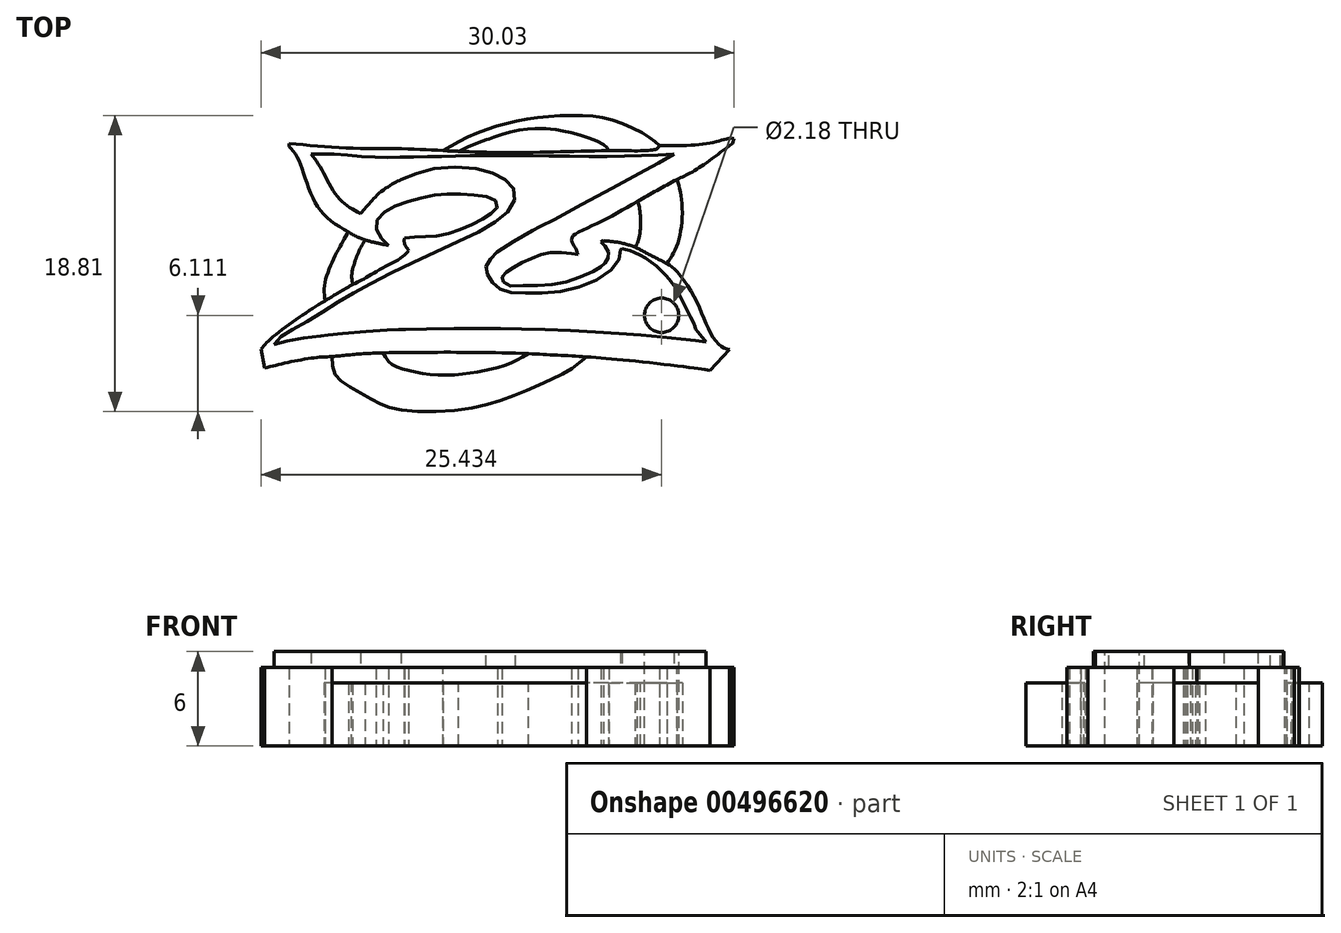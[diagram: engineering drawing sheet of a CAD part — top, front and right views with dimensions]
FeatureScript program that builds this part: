
annotation { "Feature Type Name" : "Feature", "Feature Type Description" : "" }
export const myFeature = defineFeature(function(context is Context, id is Id, definition is map)
    precondition{}
    {
        {
            var Q0;
            Q0=qCreatedBy(makeId("Top.planeOp"),FACE);
            var sketch = newSketch(context, id + "F0", { "sketchPlane" : qUnion([Q0])});
            skFitSpline(sketch, "E0", {"points": [v(13.58, 13.35) * mm, v(13.14, 12.61) * mm, v(12.53, 11.4) * mm, v(12.07, 10.03) * mm, v(12.1, 8.98) * mm], "startDerivative": vector(-2, -3.2) * mm, "endDerivative": vector(0.48, -4.3) * mm});
            skFitSpline(sketch, "E1", {"points": [v(12.1, 8.98) * mm, v(10.27, 7.8) * mm, v(8.5, 6.45) * mm, v(8.04, 5.92) * mm], "startDerivative": vector(-4.56, -2.82) * mm, "endDerivative": vector(-1.64, -2.15) * mm});
            skFitSpline(sketch, "E2", {"points": [v(8.04, 5.92) * mm, v(8.25, 4.7) * mm], "startDerivative": vector(0.2, -1.22) * mm, "endDerivative": vector(0.2, -1.22) * mm});
            skFitSpline(sketch, "E3", {"points": [v(8.25, 4.7) * mm, v(9.7, 5.06) * mm, v(11.49, 5.38) * mm, v(12.53, 5.44) * mm], "startDerivative": vector(4.05, 1.06) * mm, "endDerivative": vector(3.4, 0.09) * mm});
            skFitSpline(sketch, "E4", {"points": [v(12.53, 5.44) * mm, v(12.72, 4.35) * mm, v(13.67, 3.5) * mm, v(15.35, 2.58) * mm, v(16.7, 2.08) * mm, v(20.78, 2.08) * mm, v(23.76, 2.84) * mm, v(26.09, 3.8) * mm, v(27.8, 4.7) * mm, v(28.7, 5.43) * mm], "startDerivative": vector(0.47, -13.97) * mm, "endDerivative": vector(9.33, 8.63) * mm});
            skFitSpline(sketch, "E5", {"points": [v(28.7, 5.43) * mm, v(31.5, 5.19) * mm, v(35.57, 4.7) * mm, v(36.54, 4.55) * mm], "startDerivative": vector(7.06, -0.54) * mm, "endDerivative": vector(3.65, -0.63) * mm});
            skFitSpline(sketch, "E6", {"points": [v(36.54, 4.55) * mm, v(37.79, 5.9) * mm], "startDerivative": vector(1.1, 1.19) * mm, "endDerivative": vector(1.1, 1.19) * mm});
            skFitSpline(sketch, "E7", {"points": [v(37.79, 5.9) * mm, v(37.25, 6.09) * mm, v(36.5, 7.1) * mm, v(35.6, 9.12) * mm, v(34.36, 10.93) * mm, v(33.81, 11.36) * mm], "startDerivative": vector(-4.02, 0.8) * mm, "endDerivative": vector(-3.45, 2.2) * mm});
            skFitSpline(sketch, "E8", {"points": [v(33.81, 11.36) * mm, v(34.32, 12.19) * mm, v(34.73, 13.7) * mm, v(34.72, 15.63) * mm, v(34.45, 16.7) * mm], "startDerivative": vector(2.52, 3.62) * mm, "endDerivative": vector(-1.37, 4.33) * mm});
            skFitSpline(sketch, "E9", {"points": [v(34.45, 16.7) * mm, v(35.58, 17.26) * mm, v(37.97, 18.98) * mm], "startDerivative": vector(2.63, 1.14) * mm, "endDerivative": vector(4.28, 3.28) * mm});
            skFitSpline(sketch, "E10", {"points": [v(37.97, 18.98) * mm, v(38.07, 19.3) * mm], "startDerivative": vector(0.1, 0.31) * mm, "endDerivative": vector(0.1, 0.31) * mm});
            skFitSpline(sketch, "E11", {"points": [v(38.07, 19.3) * mm, v(37.71, 19.3) * mm, v(36.45, 18.98) * mm, v(33.34, 18.83) * mm], "startDerivative": vector(-1.85, 0.2) * mm, "endDerivative": vector(-6.74, 0.02) * mm});
            skFitSpline(sketch, "E12", {"points": [v(33.34, 18.83) * mm, v(32.6, 19.43) * mm, v(30.55, 20.4) * mm, v(28.4, 20.75) * mm, v(25.67, 20.63) * mm, v(23.4, 20.18) * mm, v(21.24, 19.43) * mm, v(19.6, 18.52) * mm], "startDerivative": vector(-6.36, 5.8) * mm, "endDerivative": vector(-11.46, -6.9) * mm});
            skFitSpline(sketch, "E13", {"points": [v(19.6, 18.52) * mm, v(17.06, 18.64) * mm, v(13.54, 18.69) * mm, v(9.8, 18.98) * mm], "startDerivative": vector(-8.25, 0.51) * mm, "endDerivative": vector(-10.4, 1.04) * mm});
            skFitSpline(sketch, "E14", {"points": [v(9.8, 18.98) * mm, v(9.8, 18.69) * mm], "startDerivative": vector(0, -0.3) * mm, "endDerivative": vector(0, -0.3) * mm});
            skFitSpline(sketch, "E15", {"points": [v(9.8, 18.78) * mm, v(10.25, 18.25) * mm, v(10.7, 17.2) * mm, v(11.3, 15.55) * mm, v(12.18, 14.3) * mm, v(13.58, 13.35) * mm], "startDerivative": vector(3.25, -3.3) * mm, "endDerivative": vector(6.7, -3.92) * mm});
            skFitSpline(sketch, "E16", {"points": [v(13.58, 13.35) * mm, v(14.49, 12.9) * mm, v(16.15, 12.5) * mm], "startDerivative": vector(1.9, -1.1) * mm, "endDerivative": vector(3.18, -0.62) * mm});
            skFitSpline(sketch, "E17", {"points": [v(16.15, 12.5) * mm, v(15.55, 13.14) * mm, v(15.36, 13.94) * mm, v(15.97, 14.68) * mm, v(17.3, 15.26) * mm, v(18.9, 15.66) * mm, v(20.42, 15.78) * mm, v(21.93, 15.65) * mm, v(22.88, 15.38) * mm, v(23.03, 14.9) * mm, v(22.6, 14.5) * mm, v(21.7, 13.94) * mm, v(20.42, 13.42) * mm, v(19.17, 13.1) * mm, v(18.1, 13.05) * mm, v(17.14, 12.96) * mm], "startDerivative": vector(-10.92, 9.75) * mm, "endDerivative": vector(-14.94, -1.84) * mm});
            skFitSpline(sketch, "E18", {"points": [v(17.14, 12.96) * mm, v(17.14, 12.64) * mm, v(17.4, 12.2) * mm], "startDerivative": vector(-0.1, -0.72) * mm, "endDerivative": vector(0.61, -0.81) * mm});
            skFitSpline(sketch, "E19", {"points": [v(17.4, 12.2) * mm, v(16.95, 11.73) * mm, v(15.68, 11.02) * mm, v(14.59, 10.39) * mm, v(13.85, 10) * mm, v(12.1, 8.98) * mm], "startDerivative": vector(-2.54, -3.12) * mm, "endDerivative": vector(-7.54, -4.52) * mm});
            skFitSpline(sketch, "E20", {"points": [v(14.63, 12.85) * mm, v(14.3, 12.21) * mm, v(13.98, 11.43) * mm, v(13.8, 10.63) * mm, v(13.85, 10) * mm], "startDerivative": vector(-1.42, -2.54) * mm, "endDerivative": vector(0.49, -2.63) * mm});
            skFitSpline(sketch, "E21", {"points": [v(12.53, 5.44) * mm, v(14.86, 5.64) * mm, v(18.8, 5.71) * mm, v(23.66, 5.67) * mm, v(28.7, 5.43) * mm], "startDerivative": vector(11.37, 1.21) * mm, "endDerivative": vector(17.86, -1.02) * mm});
            skFitSpline(sketch, "E22", {"points": [v(15.8, 5.68) * mm, v(16.21, 5.05) * mm, v(17.1, 4.65) * mm, v(18.62, 4.32) * mm, v(20.64, 4.3) * mm, v(22.39, 4.59) * mm, v(23.81, 5) * mm, v(25.02, 5.62) * mm], "startDerivative": vector(3.25, -6.46) * mm, "endDerivative": vector(8.37, 4.26) * mm});
            skFitSpline(sketch, "E23", {"points": [v(33.81, 11.36) * mm, v(32.81, 11.86) * mm, v(31.79, 12.38) * mm, v(30.8, 12.68) * mm, v(29.77, 12.8) * mm], "startDerivative": vector(-3.93, 1.93) * mm, "endDerivative": vector(-4.25, 0.35) * mm});
            skFitSpline(sketch, "E24", {"points": [v(29.77, 12.8) * mm, v(29.61, 12.7) * mm], "startDerivative": vector(-0.16, -0.09) * mm, "endDerivative": vector(-0.16, -0.09) * mm});
            skFitSpline(sketch, "E25", {"points": [v(29.61, 12.7) * mm, v(29.8, 12.53) * mm, v(30.04, 12.26) * mm, v(30.13, 11.88) * mm, v(30.06, 11.64) * mm, v(29.92, 11.43) * mm, v(29.67, 11.21) * mm, v(29.38, 10.97) * mm, v(27.99, 10.38) * mm, v(26.39, 10) * mm, v(24.65, 9.96) * mm, v(23.64, 10) * mm, v(23.37, 10.3) * mm, v(23.34, 10.47) * mm, v(23.54, 10.75) * mm, v(23.97, 11.05) * mm, v(24.6, 11.42) * mm, v(25.47, 11.77) * mm, v(26.18, 12.01) * mm, v(27.08, 12.06) * mm, v(27.84, 11.98) * mm, v(28.15, 11.94) * mm], "startDerivative": vector(5.36, -5.61) * mm, "endDerivative": vector(8.04, -1.2) * mm});
            skFitSpline(sketch, "E26", {"points": [v(28.15, 11.94) * mm, v(28, 12.3) * mm, v(27.8, 12.7) * mm, v(27.83, 13.08) * mm, v(29.2, 13.8) * mm, v(31.58, 15.1) * mm, v(34.45, 16.7) * mm], "startDerivative": vector(-1.34, 3.88) * mm, "endDerivative": vector(10.72, 5.9) * mm});
            skFitSpline(sketch, "E27", {"points": [v(31.79, 12.38) * mm, v(32, 12.84) * mm, v(32.13, 13.82) * mm, v(32.07, 14.88) * mm, v(31.94, 15.3) * mm], "startDerivative": vector(1.17, 1.95) * mm, "endDerivative": vector(-0.73, 1.87) * mm});
            skFitSpline(sketch, "E28", {"points": [v(19.6, 18.52) * mm, v(22.35, 18.42) * mm, v(26.34, 18.43) * mm, v(30.52, 18.52) * mm, v(33.15, 18.63) * mm, v(33.34, 18.83) * mm], "startDerivative": vector(12.37, -0.59) * mm, "endDerivative": vector(1.53, 3.38) * mm});
            skFitSpline(sketch, "E29", {"points": [v(30.09, 18.52) * mm, v(29.87, 18.83) * mm, v(28.01, 19.6) * mm, v(26.45, 19.9) * mm, v(25.8, 19.94) * mm, v(24.06, 19.74) * mm, v(22.49, 19.27) * mm, v(22.29, 19.22) * mm, v(20.57, 18.48) * mm], "startDerivative": vector(-1.68, 4.15) * mm, "endDerivative": vector(-13.74, -6.06) * mm});
            skSolve(sketch);
        }
        {
            var Q0;
            {var subQ0=sQuery(id+"F0.wireOp",EDGE,"E0");Q0=makeQuery(id+"F0.imprint","IMPRINT",FACE,{"disambiguationData":[TD([[makeQuery(id+"F0.imprint","IMPRINT",EDGE,{"derivedFrom":subQ0}),1.0]])]});}
            var Q1;
            {var subQ0=sQuery(id+"F0.wireOp",EDGE,"E4");Q1=makeQuery(id+"F0.imprint","IMPRINT",FACE,{"disambiguationData":[TD([[makeQuery(id+"F0.imprint","IMPRINT",EDGE,{"derivedFrom":subQ0}),1.0]])]});}
            var Q2;
            {var subQ0=sQuery(id+"F0.wireOp",EDGE,"E8");Q2=makeQuery(id+"F0.imprint","IMPRINT",FACE,{"disambiguationData":[TD([[makeQuery(id+"F0.imprint","IMPRINT",EDGE,{"derivedFrom":subQ0}),1.0]])]});}
            var Q3;
            {var subQ0=sQuery(id+"F0.wireOp",EDGE,"E12");Q3=makeQuery(id+"F0.imprint","IMPRINT",FACE,{"disambiguationData":[TD([[makeQuery(id+"F0.imprint","IMPRINT",EDGE,{"derivedFrom":subQ0}),1.0]])]});}
            extrude(context, id + "F1", {"entities" : qUnion([Q0, Q1, Q2, Q3]), "depth" : 4 * mm, "offsetDistance" : 25 * mm});
        }
        {
            var Q0;
            {var subQ11=sQuery(id+"F0.wireOp",EDGE,"E1");Q0=makeQuery(id+"F0.imprint","IMPRINT",FACE,{"disambiguationData":[TD([[makeQuery(id+"F0.imprint","IMPRINT",EDGE,{"derivedFrom":subQ11}),1.0]])]});}
            extrude(context, id + "F2", {"entities" : qUnion([Q0]), "depth" : 5 * mm, "offsetDistance" : 25 * mm});
        }
        {
            var Q0;
            Q0=makeQuery(id+"F2.opExtrude","CAP_FACE",FACE,{"disambiguationData":[OSD([sQuery(id+"F0.wireOp",EDGE,"E1"),sQuery(id+"F0.wireOp",EDGE,"E2"),sQuery(id+"F0.wireOp",EDGE,"E3"),sQuery(id+"F0.wireOp",EDGE,"E5"),sQuery(id+"F0.wireOp",EDGE,"E6"),sQuery(id+"F0.wireOp",EDGE,"E7"),sQuery(id+"F0.wireOp",EDGE,"E9"),sQuery(id+"F0.wireOp",EDGE,"E10"),sQuery(id+"F0.wireOp",EDGE,"E11"),sQuery(id+"F0.wireOp",EDGE,"E13"),sQuery(id+"F0.wireOp",EDGE,"E14"),sQuery(id+"F0.wireOp",EDGE,"E15"),sQuery(id+"F0.wireOp",EDGE,"E16"),sQuery(id+"F0.wireOp",EDGE,"E17"),sQuery(id+"F0.wireOp",EDGE,"E18"),sQuery(id+"F0.wireOp",EDGE,"E19"),sQuery(id+"F0.wireOp",EDGE,"E21"),sQuery(id+"F0.wireOp",EDGE,"E23"),sQuery(id+"F0.wireOp",EDGE,"E24"),sQuery(id+"F0.wireOp",EDGE,"E25"),sQuery(id+"F0.wireOp",EDGE,"E26"),sQuery(id+"F0.wireOp",EDGE,"E28")])],"isStart":false});
            var sketch = newSketch(context, id + "F3", { "sketchPlane" : qUnion([Q0])});
            skFitSpline(sketch, "E30", {"points": [v(14.35, 14.52) * mm, v(13.46, 15.07) * mm, v(12.6, 16.02) * mm, v(11.81, 17.45) * mm, v(11.2, 18.3) * mm], "startDerivative": vector(-3.97, 2.17) * mm, "endDerivative": vector(-2.65, 3.32) * mm});
            skFitSpline(sketch, "E31", {"points": [v(11.2, 18.3) * mm, v(12.82, 18.3) * mm, v(15.1, 18.1) * mm, v(17, 18.1) * mm, v(19.32, 18.14) * mm, v(21.84, 18.2) * mm, v(26.8, 18.18) * mm, v(31, 18.17) * mm, v(34.27, 18.3) * mm], "startDerivative": vector(15.97, 0.52) * mm, "endDerivative": vector(23.7, 1.2) * mm});
            skFitSpline(sketch, "E32", {"points": [v(34.27, 18.3) * mm, v(31.2, 16.61) * mm, v(25.81, 13.7) * mm, v(25.6, 13.61) * mm, v(23.17, 12.18) * mm, v(22.6, 11.63) * mm, v(22.32, 11.16) * mm, v(22.43, 10.66) * mm, v(22.77, 10.11) * mm, v(23.4, 9.63) * mm, v(24.65, 9.47) * mm, v(26.81, 9.55) * mm, v(29.37, 10.33) * mm, v(30.7, 11.49) * mm, v(30.87, 12.23) * mm], "startDerivative": vector(-22.34, -12.23) * mm, "endDerivative": vector(0.83, 14.09) * mm});
            skFitSpline(sketch, "E33", {"points": [v(30.87, 12.23) * mm, v(30.96, 12.31) * mm], "startDerivative": vector(0.1, 0.08) * mm, "endDerivative": vector(0.1, 0.08) * mm});
            skFitSpline(sketch, "E34", {"points": [v(30.96, 12.31) * mm, v(31.47, 12.16) * mm, v(32.4, 11.7) * mm, v(33.58, 10.76) * mm, v(34.52, 9.53) * mm, v(35.17, 8.25) * mm, v(35.6, 7.34) * mm, v(35.67, 7.15) * mm, v(36.22, 6.47) * mm, v(36.3, 6.36) * mm], "startDerivative": vector(5.3, -1.4) * mm, "endDerivative": vector(1.14, -1.67) * mm});
            skFitSpline(sketch, "E35", {"points": [v(36.3, 6.36) * mm, v(35.34, 6.5) * mm, v(32.85, 6.74) * mm, v(28.96, 7.03) * mm, v(24.45, 7.2) * mm, v(20.81, 7.22) * mm, v(16.95, 7.16) * mm, v(16.78, 7.15) * mm, v(15.34, 7.07) * mm, v(12.3, 6.8) * mm, v(12.14, 6.78) * mm, v(10.35, 6.56) * mm, v(8.88, 6.22) * mm], "startDerivative": vector(-14.7, 2.04) * mm, "endDerivative": vector(-17.73, -4.9) * mm});
            skFitSpline(sketch, "E36", {"points": [v(8.88, 6.22) * mm, v(9.41, 6.78) * mm, v(10.85, 7.6) * mm, v(12.86, 8.85) * mm, v(15.1, 10.14) * mm, v(18.8, 11.94) * mm, v(22.3, 13.6) * mm, v(23.84, 14.82) * mm, v(24.17, 15.92) * mm, v(23.5, 16.7) * mm, v(22.01, 17.31) * mm, v(18.97, 17.36) * mm, v(16.92, 16.68) * mm], "startDerivative": vector(8.79, 11.18) * mm, "endDerivative": vector(-21.95, -9.6) * mm});
            skFitSpline(sketch, "E37", {"points": [v(16.92, 16.68) * mm, v(16.37, 16.4) * mm, v(15.46, 15.75) * mm, v(14.83, 15.08) * mm, v(14.35, 14.52) * mm], "startDerivative": vector(-2.4, -1.13) * mm, "endDerivative": vector(-2.02, -2.32) * mm});
            skSolve(sketch);
        }
        {
            var Q0;
            Q0=makeQuery(id+"F3.imprint","IMPRINT",FACE,{"disambiguationData":[TD([[makeQuery(id+"F3.imprint","IMPRINT",EDGE,{"derivedFrom":sQuery(id+"F3.wireOp",EDGE,"E30")}),-1.0]])]});
            extrude(context, id + "F4", {"entities" : qUnion([Q0]), "operationType" : NewBodyOperationType.ADD, "depth" : 1 * mm, "offsetDistance" : 25 * mm});
        }
        {
            var Q0;
            Q0=makeQuery(id+"F4.opExtrude","CAP_FACE",FACE,{"disambiguationData":[OSD([sQuery(id+"F3.wireOp",EDGE,"E30"),sQuery(id+"F3.wireOp",EDGE,"E31"),sQuery(id+"F3.wireOp",EDGE,"E32"),sQuery(id+"F3.wireOp",EDGE,"E33"),sQuery(id+"F3.wireOp",EDGE,"E34"),sQuery(id+"F3.wireOp",EDGE,"E35"),sQuery(id+"F3.wireOp",EDGE,"E36"),sQuery(id+"F3.wireOp",EDGE,"E37")])],"isStart":false});
            var sketch = newSketch(context, id + "F5", { "sketchPlane" : qUnion([Q0])});
            skCircle(sketch, "E38", {"center": v(33.47, 8.06) * mm, "radius": 1.09 * mm});
            skSolve(sketch);
        }
        {
            var Q0;
            Q0 = qSketchRegion(id + "F5", true);
            extrude(context, id + "F6", {"entities" : qUnion([Q0]), "operationType" : NewBodyOperationType.REMOVE, "oppositeDirection" : true, "depth" : 25 * mm, "offsetDistance" : 25 * mm});
        }
    });
